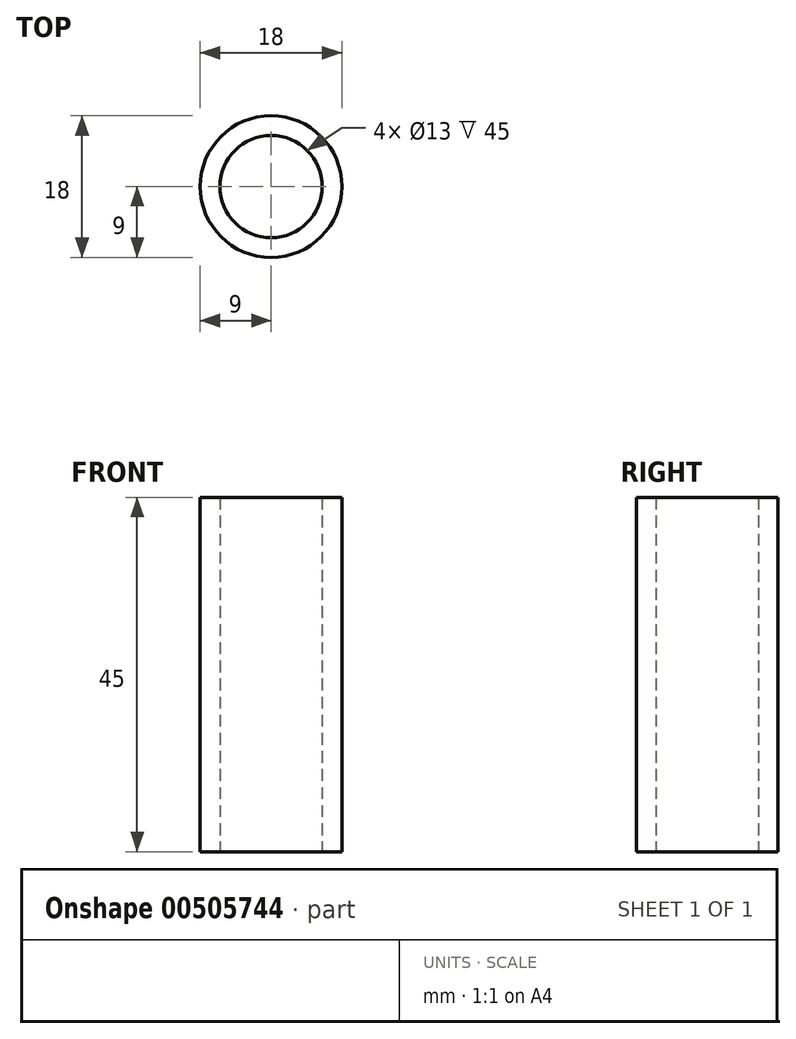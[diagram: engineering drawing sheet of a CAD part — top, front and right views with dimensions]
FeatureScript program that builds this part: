
annotation { "Feature Type Name" : "Feature", "Feature Type Description" : "" }
export const myFeature = defineFeature(function(context is Context, id is Id, definition is map)
    precondition{}
    {
        {
            var Q0;
            Q0=qCreatedBy(makeId("Top.planeOp"),FACE);
            var sketch = newSketch(context, id + "F0", { "sketchPlane" : qUnion([Q0])});
            skCircle(sketch, "E0", {"center": v(0, 0) * mm, "radius": 9 * mm});
            skCircle(sketch, "E1", {"center": v(0, 0) * mm, "radius": 6.5 * mm});
            skSolve(sketch);
        }
        {
            var Q0;
            Q0 = qSketchRegion(id + "F0", true);
            extrude(context, id + "F1", {"entities" : qUnion([Q0]), "depth" : 45 * mm});
        }
        {
            var Q0;
            Q0=qCreatedBy(makeId("Front.planeOp"),FACE);
            var sketch = newSketch(context, id + "F2", { "sketchPlane" : qUnion([Q0])});
            skLineSegment(sketch, "E2", {"start": v(-6.5, 45.22) * mm, "end": v(-21.5, 65.22) * mm});
            skLineSegment(sketch, "E3", {"start": v(-21.5, 65.22) * mm, "end": v(-26.5, 65.22) * mm});
            skLineSegment(sketch, "E4", {"start": v(-26.5, 65.22) * mm, "end": v(-26.5, 45.22) * mm});
            skLineSegment(sketch, "E5", {"start": v(-26.5, 45.22) * mm, "end": v(-6.5, 45.22) * mm});
            skLineSegment(sketch, "E6", {"start": v(0, 0) * mm, "end": v(0, 75.15) * mm, "construction": true});
            skSolve(sketch);
        }
        {
            var Q0;
            Q0=sQuery(id+"F2.wireOp",EDGE,"E2");
            var Q1;
            Q1=sQuery(id+"F2.wireOp",EDGE,"E3");
            var Q2;
            Q2=sQuery(id+"F2.wireOp",EDGE,"E4");
            var Q3;
            Q3=sQuery(id+"F2.wireOp",EDGE,"E5");
            var Q4;
            Q4=sQuery(id+"F2.wireOp",EDGE,"E6");
            revolve(context, id + "F3", {"bodyType" : ToolBodyType.SURFACE, "surfaceEntities" : qUnion([Q0, Q1, Q2, Q3]), "axis" : qUnion([Q4]), "revolveType" : RevolveType.FULL});
        }
    });
